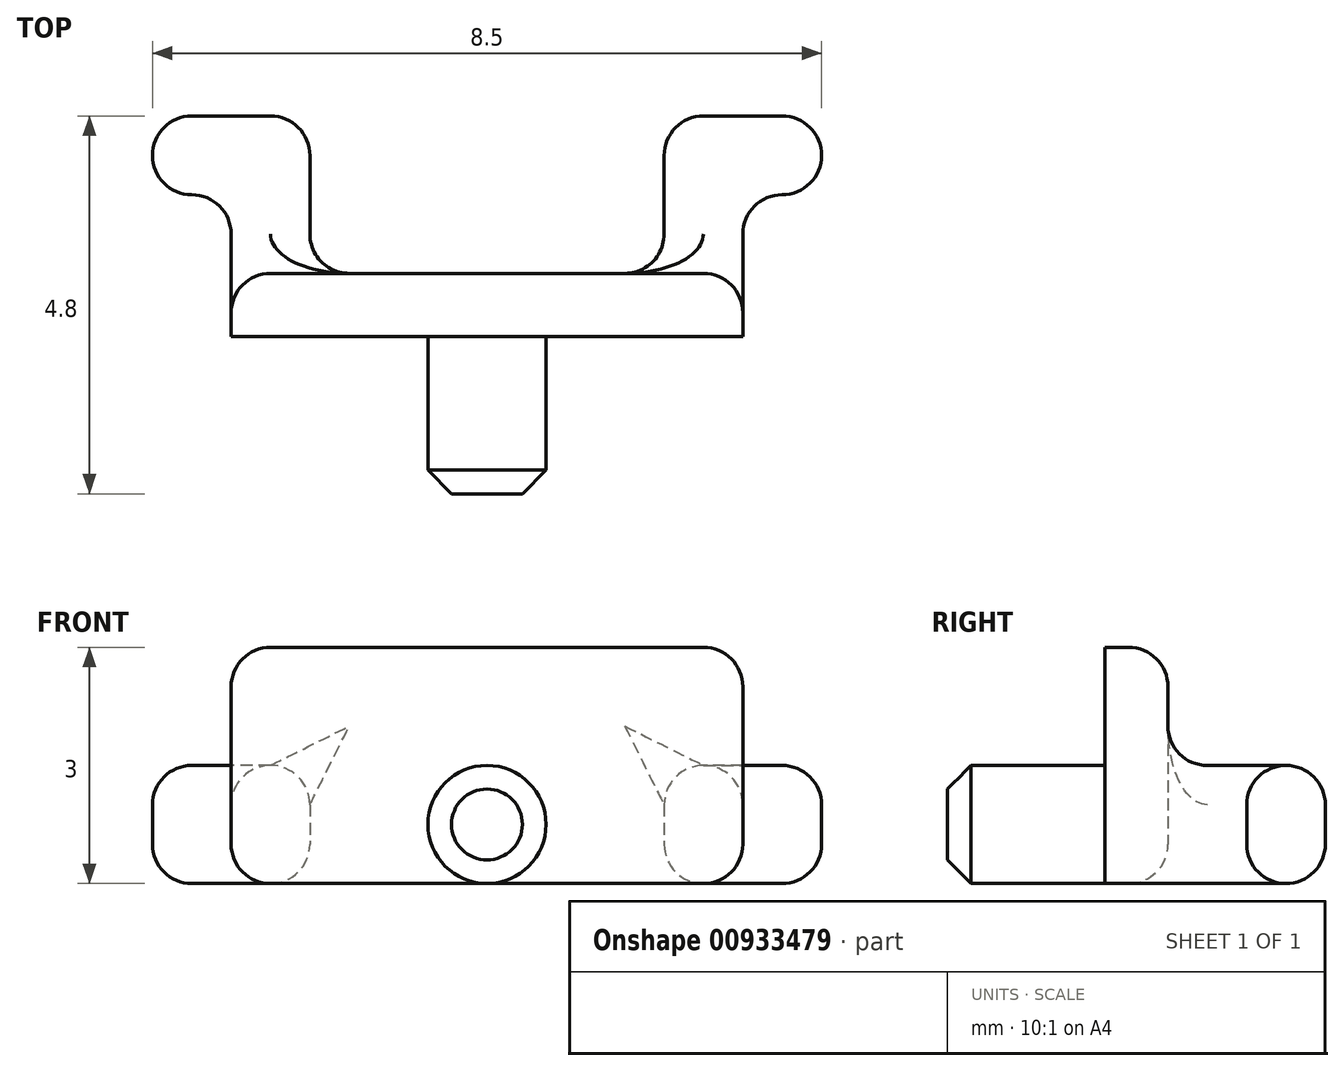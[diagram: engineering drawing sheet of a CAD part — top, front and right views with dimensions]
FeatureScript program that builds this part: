
annotation { "Feature Type Name" : "Feature", "Feature Type Description" : "" }
export const myFeature = defineFeature(function(context is Context, id is Id, definition is map)
    precondition{}
    {
        {
            var Q0;
            Q0=qCreatedBy(makeId("Top.planeOp"),FACE);
            var sketch = newSketch(context, id + "F0", { "sketchPlane" : qUnion([Q0])});
            skLineSegment(sketch, "E0", {"start": v(-3.25, 0) * mm, "end": v(-0.75, 0) * mm});
            skPoint(sketch, "E1", {"position": v(0, 0) * mm});
            skLineSegment(sketch, "E2", {"start": v(0, -3) * mm, "end": v(0, 7.11) * mm, "construction": true});
            skLineSegment(sketch, "E3", {"start": v(2.25, 1.3) * mm, "end": v(2.25, 2.3) * mm});
            skLineSegment(sketch, "E4", {"start": v(-2.25, 1.3) * mm, "end": v(-2.25, 2.3) * mm});
            skLineSegment(sketch, "E5", {"start": v(-1.75, 0.8) * mm, "end": v(1.75, 0.8) * mm});
            skPoint(sketch, "E6", {"position": v(0, 0.8) * mm});
            skLineSegment(sketch, "E7", {"start": v(-2.75, 2.8) * mm, "end": v(-3.75, 2.8) * mm});
            skLineSegment(sketch, "E8", {"start": v(2.75, 2.8) * mm, "end": v(3.75, 2.8) * mm});
            skLineSegment(sketch, "E9", {"start": v(-4.25, 2.3) * mm, "end": v(-4.25, 2.3) * mm});
            skLineSegment(sketch, "E10", {"start": v(-3.75, 1.8) * mm, "end": v(-3.75, 1.8) * mm});
            skLineSegment(sketch, "E11", {"start": v(-3.25, 1.3) * mm, "end": v(-3.25, 0) * mm});
            skLineSegment(sketch, "E12", {"start": v(4.25, 2.3) * mm, "end": v(4.25, 2.3) * mm});
            skLineSegment(sketch, "E13", {"start": v(3.75, 1.8) * mm, "end": v(3.75, 1.8) * mm});
            skLineSegment(sketch, "E14", {"start": v(3.25, 1.3) * mm, "end": v(3.25, 0) * mm});
            skPoint(sketch, "E15.visualSharp", {"position": v(-2.25, 0.8) * mm});
            skArc(sketch, "E15.filletArc", {"start": v(-2.25, 1.3) * mm, "mid": v(-2.1, 0.95) * mm, "end": v(-1.75, 0.8) * mm});
            skPoint(sketch, "E16.visualSharp", {"position": v(2.25, 0.8) * mm});
            skArc(sketch, "E16.filletArc", {"start": v(1.75, 0.8) * mm, "mid": v(2.1, 0.95) * mm, "end": v(2.25, 1.3) * mm});
            skPoint(sketch, "E17.visualSharp", {"position": v(3.25, 1.8) * mm});
            skArc(sketch, "E17.filletArc", {"start": v(3.75, 1.8) * mm, "mid": v(3.4, 1.65) * mm, "end": v(3.25, 1.3) * mm});
            skPoint(sketch, "E18.visualSharp", {"position": v(-3.25, 1.8) * mm});
            skArc(sketch, "E18.filletArc", {"start": v(-3.25, 1.3) * mm, "mid": v(-3.4, 1.65) * mm, "end": v(-3.75, 1.8) * mm});
            skPoint(sketch, "E19.visualSharp", {"position": v(-2.25, 2.8) * mm});
            skArc(sketch, "E19.filletArc", {"start": v(-2.25, 2.3) * mm, "mid": v(-2.4, 2.65) * mm, "end": v(-2.75, 2.8) * mm});
            skPoint(sketch, "E20.visualSharp", {"position": v(2.25, 2.8) * mm});
            skArc(sketch, "E20.filletArc", {"start": v(2.75, 2.8) * mm, "mid": v(2.4, 2.65) * mm, "end": v(2.25, 2.3) * mm});
            skPoint(sketch, "E21.visualSharp", {"position": v(4.25, 2.8) * mm});
            skArc(sketch, "E21.filletArc", {"start": v(4.25, 2.3) * mm, "mid": v(4.1, 2.65) * mm, "end": v(3.75, 2.8) * mm});
            skPoint(sketch, "E22.visualSharp", {"position": v(4.25, 1.8) * mm});
            skArc(sketch, "E22.filletArc", {"start": v(3.75, 1.8) * mm, "mid": v(4.1, 1.95) * mm, "end": v(4.25, 2.3) * mm});
            skPoint(sketch, "E23.visualSharp", {"position": v(-4.25, 2.8) * mm});
            skArc(sketch, "E23.filletArc", {"start": v(-3.75, 2.8) * mm, "mid": v(-4.1, 2.65) * mm, "end": v(-4.25, 2.3) * mm});
            skPoint(sketch, "E24.visualSharp", {"position": v(-4.25, 1.8) * mm});
            skArc(sketch, "E24.filletArc", {"start": v(-4.25, 2.3) * mm, "mid": v(-4.1, 1.95) * mm, "end": v(-3.75, 1.8) * mm});
            skLineSegment(sketch, "E25.top", {"start": v(-0.75, -2) * mm, "end": v(0.75, -2) * mm});
            skLineSegment(sketch, "E25.left", {"start": v(-0.75, 0) * mm, "end": v(-0.75, -2) * mm});
            skLineSegment(sketch, "E25.right", {"start": v(0.75, 0) * mm, "end": v(0.75, -2) * mm});
            skPoint(sketch, "E26", {"position": v(0, -2) * mm});
            skLineSegment(sketch, "E27.trimOffspring", {"start": v(0.75, 0) * mm, "end": v(3.25, 0) * mm});
            skSolve(sketch);
        }
        {
            var Q0;
            Q0=qSketchRegion(id+"F0",true);
            extrude(context, id + "F1", {"entities" : qUnion([Q0]), "depth" : 1.5 * mm, "offsetDistance" : 25 * mm});
        }
        {
            var Q0;
            Q0=makeQuery(id+"F1.opExtrude","CAP_FACE",FACE,{"disambiguationData":[OSD([sQuery(id+"F0.wireOp",EDGE,"E0"),sQuery(id+"F0.wireOp",EDGE,"6YUp3G7D-HScl-yHn5-GseC-h8JY3a3RTnfq"),sQuery(id+"F0.wireOp",EDGE,"Xoj59s7T-2QtX-ZDX5-LiLJ-oQHR1xyVejqm"),sQuery(id+"F0.wireOp",EDGE,"Zc0sCTJD-TUej-OjTx-Aevo-d0EqPVeEhSTX"),sQuery(id+"F0.wireOp",EDGE,"E3"),sQuery(id+"F0.wireOp",EDGE,"E4"),sQuery(id+"F0.wireOp",EDGE,"fb0ed693-0343-43f7-9de8-dc647e30bef6.trimOffspring"),sQuery(id+"F0.wireOp",EDGE,"E5"),sQuery(id+"F0.wireOp",EDGE,"E7"),sQuery(id+"F0.wireOp",EDGE,"E8"),sQuery(id+"F0.wireOp",EDGE,"E15.filletArc"),sQuery(id+"F0.wireOp",EDGE,"E16.filletArc"),sQuery(id+"F0.wireOp",EDGE,"e3a1806a-2c86-475e-80ef-7f3d2f1d7afe.filletArc"),sQuery(id+"F0.wireOp",EDGE,"E17.filletArc"),sQuery(id+"F0.wireOp",EDGE,"63802826-9469-4e69-9e87-4bd683e02e6c.filletArc"),sQuery(id+"F0.wireOp",EDGE,"E18.filletArc"),sQuery(id+"F0.wireOp",EDGE,"E19.filletArc"),sQuery(id+"F0.wireOp",EDGE,"E20.filletArc"),sQuery(id+"F0.wireOp",EDGE,"E21.filletArc"),sQuery(id+"F0.wireOp",EDGE,"E22.filletArc"),sQuery(id+"F0.wireOp",EDGE,"E23.filletArc"),sQuery(id+"F0.wireOp",EDGE,"E24.filletArc")])],"isStart":false});
            var sketch = newSketch(context, id + "F2", { "sketchPlane" : qUnion([Q0])});
            skLineSegment(sketch, "E28.0", {"start": v(-3.25, 0) * mm, "end": v(-3.25, 0) * mm});
            skLineSegment(sketch, "E29.0", {"start": v(-3.25, 0) * mm, "end": v(-3.25, 0.8) * mm});
            skLineSegment(sketch, "E30.0", {"start": v(3.25, 0.8) * mm, "end": v(3.25, 0) * mm});
            skLineSegment(sketch, "E31", {"start": v(-3.25, 0.8) * mm, "end": v(3.25, 0.8) * mm});
            skLineSegment(sketch, "E32.0", {"start": v(-3.25, 0) * mm, "end": v(3.25, 0) * mm});
            skPoint(sketch, "E33.orphan", {"position": v(-0.75, 0) * mm});
            skSolve(sketch);
        }
        {
            var Q0;
            Q0=qSketchRegion(id+"F2",true);
            extrude(context, id + "F3", {"entities" : qUnion([Q0]), "operationType" : NewBodyOperationType.ADD, "depth" : 1.5 * mm, "offsetDistance" : 25 * mm});
        }
        {
            var Q0;
            {var subQ1=sQuery(id+"F0.wireOp",EDGE,"E14");var subQ3=sQuery(id+"F2.wireOp",EDGE,"E31");Q0=makeQuery(id+"F3.boolean.opBoolean","SPLIT",EDGE,{"disambiguationData":[TD([makeQuery(id+"F1.opExtrude","SWEPT_FACE",FACE,{"disambiguationData":[OSD([subQ1])]})])],"derivedFrom":makeQuery(id+"F3.opExtrude","CAP_EDGE",EDGE,{"disambiguationData":[OSD([subQ3])],"isStart":true})});}
            var Q1;
            {var subQ0=sQuery(id+"F0.wireOp",EDGE,"E11");var subQ3=sQuery(id+"F2.wireOp",EDGE,"E31");Q1=makeQuery(id+"F3.boolean.opBoolean","SPLIT",EDGE,{"disambiguationData":[TD([makeQuery(id+"F1.opExtrude","SWEPT_FACE",FACE,{"disambiguationData":[OSD([subQ0])]})])],"derivedFrom":makeQuery(id+"F3.opExtrude","CAP_EDGE",EDGE,{"disambiguationData":[OSD([subQ3])],"isStart":true})});}
            fillet(context, id + "F4", {"entities" : qUnion([Q0, Q1]), "radius" : 0.5 * mm, "tangentPropagation" : true, "defaultsChanged" : true, "vertexSettings" : [], "allowEdgeOverflow" : false});
        }
        {
            var Q0;
            Q0=makeQuery(id+"F3.opExtrude","CAP_EDGE",EDGE,{"disambiguationData":[OSD([sQuery(id+"F2.wireOp",EDGE,"E31")])],"isStart":false});
            var Q1;
            Q1=makeQuery(id+"F3.opExtrude","CAP_EDGE",EDGE,{"disambiguationData":[OSD([sQuery(id+"F2.wireOp",EDGE,"E29.0")])],"isStart":false});
            var Q2;
            Q2=makeQuery(id+"F3.opExtrude","CAP_EDGE",EDGE,{"disambiguationData":[OSD([sQuery(id+"F2.wireOp",EDGE,"E30.0")])],"isStart":false});
            var Q3;
            Q3=makeQuery(id+"F1.opExtrude","CAP_EDGE",EDGE,{"disambiguationData":[OSD([sQuery(id+"F0.wireOp",EDGE,"E8")])],"isStart":false});
            var Q4;
            Q4=makeQuery(id+"F1.opExtrude","CAP_EDGE",EDGE,{"disambiguationData":[OSD([sQuery(id+"F0.wireOp",EDGE,"E7")])],"isStart":false});
            var Q5;
            Q5=makeQuery(id+"F1.opExtrude","CAP_EDGE",EDGE,{"disambiguationData":[OSD([sQuery(id+"F0.wireOp",EDGE,"E5")])],"isStart":true});
            fillet(context, id + "F5", {"entities" : qUnion([Q0, Q1, Q2, Q3, Q4, Q5]), "radius" : 0.5 * mm, "tangentPropagation" : true, "defaultsChanged" : false, "vertexSettings" : [], "allowEdgeOverflow" : false});
        }
        {
            var Q0;
            Q0=makeQuery(id+"F1.opExtrude","CAP_EDGE",EDGE,{"disambiguationData":[OSD([sQuery(id+"F0.wireOp",EDGE,"E25.left")])],"isStart":false});
            var Q1;
            Q1=makeQuery(id+"F1.opExtrude","CAP_EDGE",EDGE,{"disambiguationData":[OSD([sQuery(id+"F0.wireOp",EDGE,"E25.right")])],"isStart":false});
            var Q2;
            Q2=makeQuery(id+"F1.opExtrude","CAP_EDGE",EDGE,{"disambiguationData":[OSD([sQuery(id+"F0.wireOp",EDGE,"E25.left")])],"isStart":true});
            var Q3;
            Q3=makeQuery(id+"F1.opExtrude","CAP_EDGE",EDGE,{"disambiguationData":[OSD([sQuery(id+"F0.wireOp",EDGE,"E25.right")])],"isStart":true});
            fillet(context, id + "F6", {"entities" : qUnion([Q0, Q1, Q2, Q3]), "tangentPropagation" : true, "radius" : 0.75 * mm, "defaultsChanged" : false, "vertexSettings" : [], "allowEdgeOverflow" : false});
        }
        {
            var Q0;
            Q0=makeQuery(id+"F6.opFillet","BLEND_EDGE",EDGE,{"blendedFrom":[makeQuery(id+"F1.opExtrude","CAP_EDGE",EDGE,{"disambiguationData":[OSD([sQuery(id+"F0.wireOp",EDGE,"E25.left")])],"isStart":true}),makeQuery(id+"F1.opExtrude","SWEPT_FACE",FACE,{"disambiguationData":[OSD([sQuery(id+"F0.wireOp",EDGE,"E25.top")])]})],"blendedInto":[makeQuery(id+"F1.opExtrude","SWEPT_FACE",FACE,{"disambiguationData":[OSD([sQuery(id+"F0.wireOp",EDGE,"E25.top")])]})]});
            chamfer(context, id + "F7", {"entities" : qUnion([Q0]), "width" : 0.3 * mm, "tangentPropagation" : true});
        }
    });
